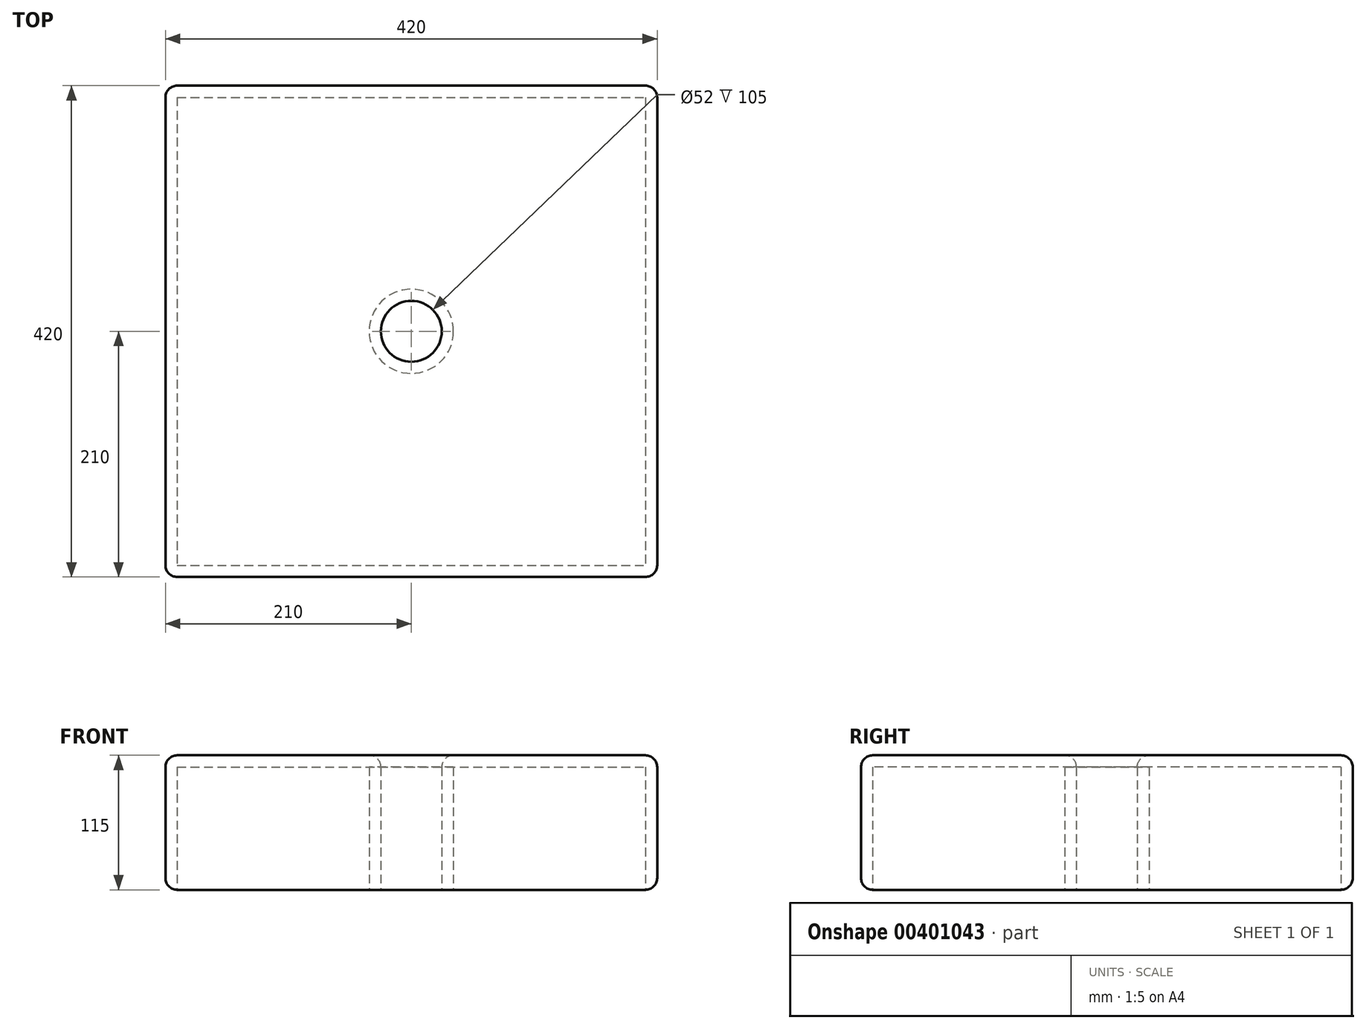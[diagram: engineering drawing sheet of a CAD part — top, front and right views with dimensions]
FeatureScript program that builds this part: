
annotation { "Feature Type Name" : "Feature", "Feature Type Description" : "" }
export const myFeature = defineFeature(function(context is Context, id is Id, definition is map)
    precondition{}
    {
        {
            var Q0;
            Q0=qCreatedBy(makeId("Top.planeOp"),FACE);
            var sketch = newSketch(context, id + "F0", { "sketchPlane" : qUnion([Q0])});
            skLineSegment(sketch, "E0.bottom", {"start": v(-210, 210) * mm, "end": v(210, 210) * mm});
            skLineSegment(sketch, "E0.top", {"start": v(-210, -210) * mm, "end": v(210, -210) * mm});
            skLineSegment(sketch, "E0.left", {"start": v(-210, 210) * mm, "end": v(-210, -210) * mm});
            skLineSegment(sketch, "E0.right", {"start": v(210, 210) * mm, "end": v(210, -210) * mm});
            skCircle(sketch, "E1", {"center": v(0, 0) * mm, "radius": 26 * mm});
            skSolve(sketch);
        }
        {
            var Q0;
            Q0=makeQuery(id+"F0.imprint","IMPRINT",FACE,{"disambiguationData":[TD([[makeQuery(id+"F0.imprint","IMPRINT",EDGE,{"derivedFrom":sQuery(id+"F0.wireOp",EDGE,"E0.bottom")}),-1.0]])]});
            extrude(context, id + "F1", {"entities" : qUnion([Q0]), "depth" : 115 * mm});
        }
        {
            var Q0;
            Q0=makeQuery(id+"F1.opExtrude","CAP_FACE",FACE,{"disambiguationData":[OSD([sQuery(id+"F0.wireOp",EDGE,"E0.bottom"),sQuery(id+"F0.wireOp",EDGE,"E0.top"),sQuery(id+"F0.wireOp",EDGE,"E0.left"),sQuery(id+"F0.wireOp",EDGE,"E0.right"),sQuery(id+"F0.wireOp",EDGE,"E1")])],"isStart":true});
            shell(context, id + "F2", {"entities" : qUnion([Q0]), "thickness" : 10 * mm});
        }
        {
            var Q0;
            Q0=makeQuery(id+"F1.opExtrude","SWEPT_FACE",FACE,{"disambiguationData":[OSD([sQuery(id+"F0.wireOp",EDGE,"E0.right")])]});
            var Q1;
            Q1=makeQuery(id+"F1.opExtrude","SWEPT_FACE",FACE,{"disambiguationData":[OSD([sQuery(id+"F0.wireOp",EDGE,"E0.bottom")])]});
            var Q2;
            Q2=makeQuery(id+"F1.opExtrude","SWEPT_FACE",FACE,{"disambiguationData":[OSD([sQuery(id+"F0.wireOp",EDGE,"E0.left")])]});
            var Q3;
            Q3=makeQuery(id+"F1.opExtrude","SWEPT_FACE",FACE,{"disambiguationData":[OSD([sQuery(id+"F0.wireOp",EDGE,"E0.top")])]});
            var Q4;
            Q4=makeQuery(id+"F1.opExtrude","CAP_FACE",FACE,{"disambiguationData":[OSD([sQuery(id+"F0.wireOp",EDGE,"E0.bottom"),sQuery(id+"F0.wireOp",EDGE,"E0.top"),sQuery(id+"F0.wireOp",EDGE,"E0.left"),sQuery(id+"F0.wireOp",EDGE,"E0.right"),sQuery(id+"F0.wireOp",EDGE,"E1")])],"isStart":false});
            fillet(context, id + "F3", {"entities" : qUnion([Q0, Q1, Q2, Q3, Q4]), "radius" : 10 * mm, "tangentPropagation" : true, "allowEdgeOverflow" : false});
        }
    });
